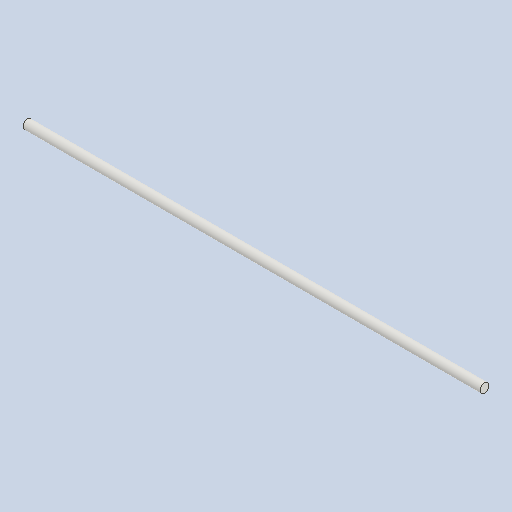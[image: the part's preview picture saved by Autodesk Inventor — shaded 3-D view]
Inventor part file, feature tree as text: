
AUTODESK INVENTOR PART (.ipt)
format: ipt  version: 2023 (Build 270158000, 158)  size: 75,264 bytes
history: native  units: mm
features: other x3, revolve x1
ambient origin geometry x6: Origin, XZ Plane, XY Plane, X Axis, Y Axis, Z Axis
bodies: Solid1 (feature_tree)
feature tree (4):
  revolve  "Revolution1"  [1 undecoded]
  other  "Start Plane"
  other  "Origin point"
  other  "Main Sketch"
note: 1 required parameter value undecoded (feature->parameter linkage not recoverable at this tier; creation-order binding heuristic only, values carry confidence <= 0.55)
